# Revit family: 18-70-003 DN200 DN PN10 and 16
name_source: partatom
category: Pipe Accessories
units: mm (PartAtom-declared; Revit-internal decimal feet)

## family parameters
Always vertical = Yes
Cut with Voids When Loaded = No
Part Type = Valve - Breaks Into
Round Connector Dimension = Use Diameter
Shared = No
Work Plane-Based = No

## types (2) — shared parameters
1 = 1 mm  [stored 0.00328084 ft]
20 = 20 mm  [stored 0.0656168 ft]
27 = 27 mm  [stored 0.0885827 ft]
5 = 5 mm  [stored 0.0164042 ft]
50 = 50 mm  [stored 0.164042 ft]
Body_H = 220 mm  [stored 0.721785 ft]
Bore_R = 100 mm  [stored 0.328084 ft]
DN = 200 mm  [stored 0.656168 ft]
DN200_PN10 = 18-200-70-0040000099
DN200_PN16 = 18-200-70-0140000099
Description_ = AVK COMBI-CROSS, FLANGED, 4 OUTLETS, PN10/16
Dh = 295 mm  [stored 0.967848 ft]
F = 12 mm  [stored 0.0393701 ft]
F1 = 14 mm  [stored 0.0459318 ft]
F2 = 47 mm  [stored 0.154199 ft]
F3 = 35 mm  [stored 0.114829 ft]
FL_R = 200 mm  [stored 0.656168 ft]
FL_T = 20 mm  [stored 0.0656168 ft]
H = 490 mm  [stored 1.60761 ft]
H1 = 365 mm  [stored 1.19751 ft]
H3 = 660 mm  [stored 2.16535 ft]
H3-H = 170 mm  [stored 0.557743 ft]
L = 750 mm  [stored 2.46063 ft]
L-L1 = 141 mm  [stored 0.462598 ft]
L1 = 468 mm  [stored 1.53543 ft]
L2 = 223 mm  [stored 0.731627 ft]
L5 = 300 mm  [stored 0.984252 ft]
L6 = 267 mm  [stored 0.875984 ft]
L_half = 188 mm
OD = 170 mm  [stored 0.557743 ft]
OD1 = 94 mm
OD2 = 103 mm
P1 = 331 mm  [stored 1.08596 ft]
Raised_R = 132 mm
Raised_dis = 3 mm  [stored 0.00984252 ft]
Search_table = 18-70-003 DN200 DN PN10 and 16
URL_product_pages = https://www.avkvalves.com
W = 170 mm  [stored 0.557743 ft]
arc = 245 mm  [stored 0.803806 ft]
arc1 = 78 mm
arc2 = 156 mm
body_dim1 = 162 mm
main_dim1 = 125 mm  [stored 0.410105 ft]
tp bore = 50 mm  [stored 0.164042 ft]
zero-valued in all types: Default Elevation

## type names (no varying parameters)
- DN200_PN10
- DN200_PN16

note: [stored X ft] marks values corroborated as IEEE doubles in the binary element streams (Revit-internal decimal feet)

## geometry (parser evidence)
native form markers: Sweep x6
no freeform markers — native parametric forms only
